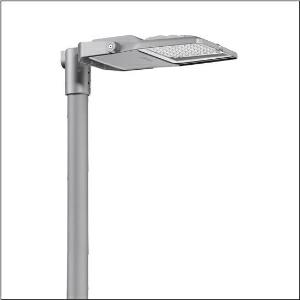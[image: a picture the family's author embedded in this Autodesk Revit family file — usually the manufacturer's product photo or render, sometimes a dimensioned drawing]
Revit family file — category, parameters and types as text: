
# Revit family: floodlight_fl_21_iq_mini___pl52_5xa7771c2d3a_33da
name_source: partatom
category: Lighting Fixtures
units: mm (PartAtom-declared; Revit-internal decimal feet)

## family parameters
Cut with Voids When Loaded = No
Host = Face
Light Source = No
Part Type = Normal
Room Calculation Point = No
Round Connector Dimension = Use Diameter
Shared = No

## types (1)
- --- (1 x LED, 12210 lm, 87.2 W, 3000K)
    Apparent Load = 87 VA
    CIE Flux Codes = 26 60 98 100 100
    Color Rendering = 70
    Color Temperature = 3000K
    Default Elevation = 1800 mm
    Description = Floodlight FL 21 iQ mini, floodlight, primary light control with lens, of PMMA, primary optical cover: protective disc, of toughened safety glass, transparent, light distribution: PL52, light emission: direct distribution, installation type: surface-mounted, LED, High Power LED, rated luminous flux: 12.210lm, luminous efficacy: 140lm/W, light colour: 730, colour temperature: 3000K, control: Auto-Match, Temp-Guard, Lumen-Switch, Night-Set, Smart-Wire, Light-Fading, Desk-Remote (wireless, voltage-free reading and setting of iQ features in the workshop via application-optimized NFC function/RFID function), optimised constant luminous flux control (CLO 2.0), with terminal, 6-pole, mains connection: 220..240V, AC, 50/60Hz, start of lifetime: 87W, end of service life: 92W, reduction: 40W, luminaire housing, of diecast aluminium, powder-coated, Siteco® metallic grey (DB 702S), corrosivity category C5 mid according to DIN EN ISO 12944, sealing non-destructively replaceable, please order mast flange separately, mast bracket, of steel, galvanised, powder-coated, Siteco® metallic grey (DB 702S), protection rating (complete): IP66, insulation class (complete): insulation class II (safety insulation), certification: CE, ENEC, VDE, protection symbol: D, impact resistance: IK08, permissible operating ambient temperature: -40..+40°C, permissible operating ambient temperature for outdoor applications: -40..+50°C, standard: DIN EN 12944, LABS conformity tested according to VDMA 24364:2018-05, packaging unit: 1 piece

Light Distribution: PL52
    Height = 70 mm
    Lamp = 1 x LED
    Lamp Light Flux = 12210 lm
    Lamp Power = 87.2 W
    Lamp count = 1
    Length = 485 mm
    Luminous efficacy = 140 lm/W
    Manufacturer = Siteco
    ModVariant = No
    Model = 5XA7771C2D3A
    Number of Poles = 1
    OnlyDefault = Yes
    Power Factor = 1
    Product Name = Floodlight FL 21 iQ mini | PL52
    Product group = floodlight | pylon annexe
    ProductGroupID = 6200
    Protection Class = Protection class II
    Protection Degree = IP 66
    RLX_Detail_Level = 1
    RLX_Emergency_Light_Flux = 0 lm
    RLX_Emergency_Type = 0
    RLX_Emergency_Type_DB = No
    RlxData = <blob elided: 101441 chars, md5=283c4f52>
    Socket = socket
    Standby Power = 0 W
    System Light Flux = 12210 lm
    System Power = 87 W
    Type Comments = factory setting: luminous flux: 100 % | dim-lin: 254 | 456 mA
    Type Image = l_1007125.jpg
    URL = http://relux.com
    VarID = @adj_096855
    Voltage = 0 V
    Weight = 0.00 kg
    Width = 337 mm

## geometry (parser evidence)
native form markers: Blend x4, Sweep x13
no freeform markers — native parametric forms only
